# Revit family: Pressure_Reducing_Valves-Acorn-Controls-RV03B_Series
name_source: partatom
category: Pipe Accessories
units: mm (PartAtom-declared; Revit-internal decimal feet)

## family parameters
Always vertical = Yes
Cut with Voids When Loaded = No
OmniClass Number = 23.65.55.14.17
OmniClass Title = Adjusting/Controlling Valves for Liquid Services
Part Type = Valve - Breaks Into
Round Connector Dimension = Use Diameter
Shared = No
Work Plane-Based = No

## types (2) — shared parameters
A Dimension = 8 1/2"
Adjustable Pressure Range = 10-75 PSI (69-517 kPa)
Assembly Code = D2090900
B Dimension = 14 3/8"
Body Material = Metal-Acorn-Lead Free Brass
Bonnet Material = Metal-Acorn-UV Resistant Material
C Dimension = 4 1/2"
D Dimension = 4"
Description = Pressure Reducing Valves
E Dimension = 1 7/8"
F Dimension = 2 1/4"
Factory Preset = 50±5 PSI (345kPa)
IAPMO Compliance = Comply with the national lead-free law, ASSE 1003 & NSF-61.
Manufacturer = Acorn
P0 Plastic = Yes
PH Plastic HP - High Pressure Spring = No
Pressure Rating = 400 PSI (2758 kPa)
S0 Steel = No
SH Steel HP - High Pressure Spring = No
Temperature Rating = 180°F (82.2°C)
URL = https://www.acorneng.com
cUPC Compliant = Yes

## per-type parameters (varying)
| type | Connection Inlet Description | Connection Outlet Description | Valve Size |
| RV03B0-70 | 2 1/2" Inlet Connection | 2 1/2" Outlet Connection | 2 1/2" |
| RV03B0-80 | 3" Inlet Connection | 3" Outlet Connection | 3" |

note: column(s) folded — value = type name in every type: Model

## geometry (parser evidence)
native form markers: Sweep x3
no freeform markers — native parametric forms only
